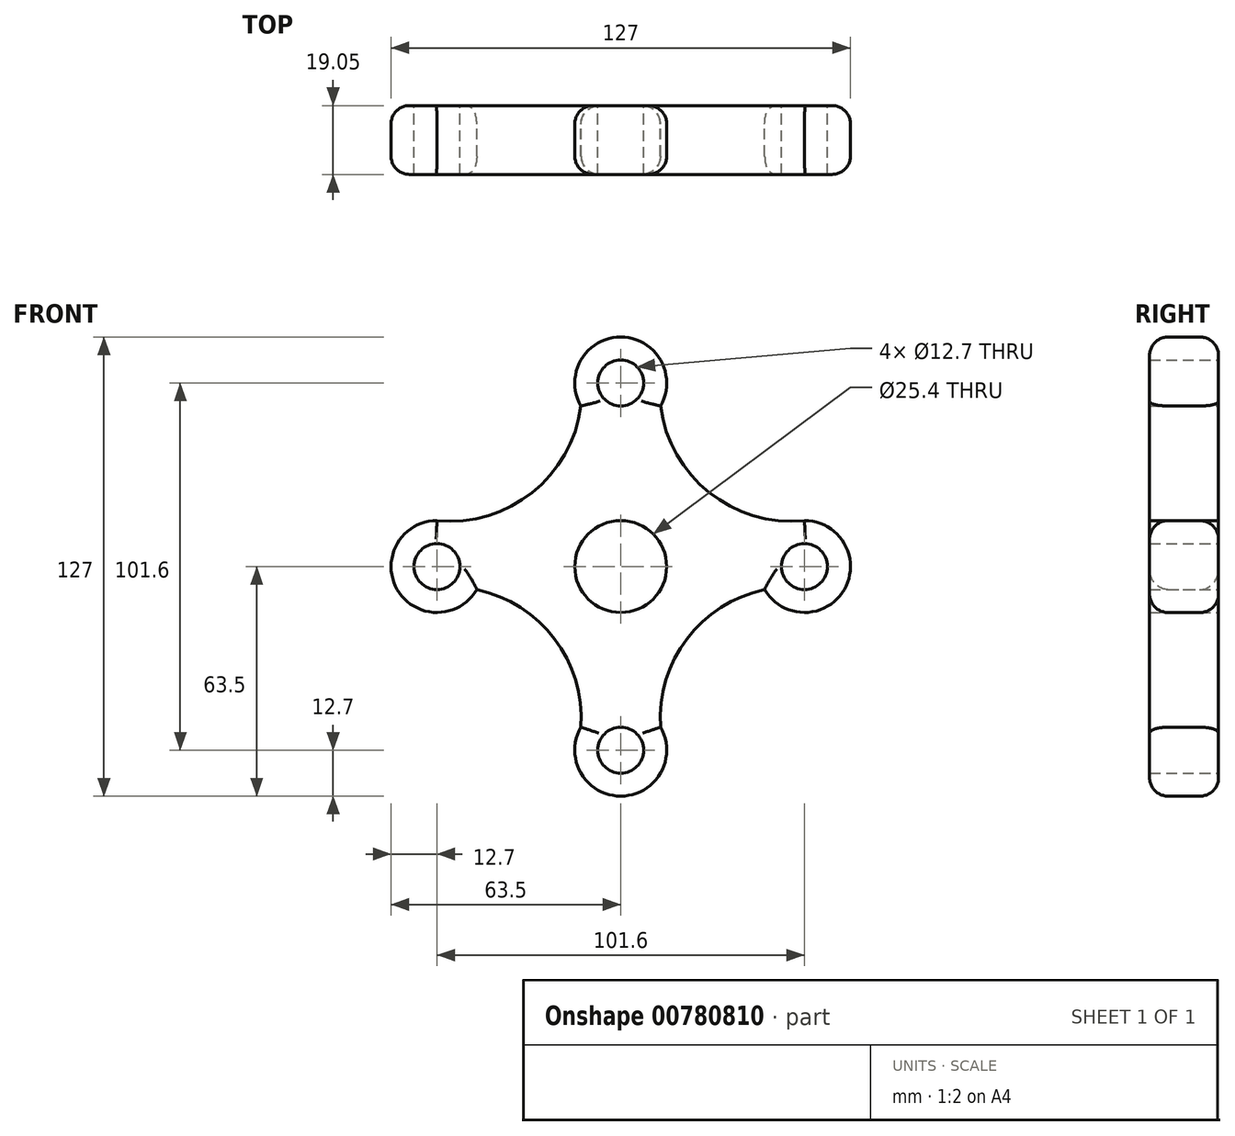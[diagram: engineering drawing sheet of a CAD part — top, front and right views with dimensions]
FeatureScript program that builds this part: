
annotation { "Feature Type Name" : "Feature", "Feature Type Description" : "" }
export const myFeature = defineFeature(function(context is Context, id is Id, definition is map)
    precondition{}
    {
        {
            var Q0;
            Q0=qCreatedBy(makeId("Front.planeOp"),FACE);
            var sketch = newSketch(context, id + "F0", { "sketchPlane" : qUnion([Q0])});
            skCircle(sketch, "E0", {"center": v(0, 0) * mm, "radius": 12.7 * mm});
            skCircle(sketch, "E1", {"center": v(0, 50.8) * mm, "radius": 6.35 * mm});
            skCircle(sketch, "E2", {"center": v(50.8, 0) * mm, "radius": 6.35 * mm});
            skCircle(sketch, "E3", {"center": v(0, -50.8) * mm, "radius": 6.35 * mm});
            skCircle(sketch, "E4", {"center": v(-50.8, 0) * mm, "radius": 6.35 * mm});
            skCircle(sketch, "E5", {"center": v(-50.8, 0) * mm, "radius": 12.7 * mm});
            skCircle(sketch, "E6", {"center": v(0, 50.8) * mm, "radius": 12.7 * mm});
            skCircle(sketch, "E7", {"center": v(50.8, 0) * mm, "radius": 12.7 * mm});
            skCircle(sketch, "E8", {"center": v(0, -50.8) * mm, "radius": 12.7 * mm});
            skLineSegment(sketch, "E9", {"start": v(0, 50.8) * mm, "end": v(0, 50.8) * mm});
            skArc(sketch, "E10", {"start": v(-50.8, 12.7) * mm, "mid": v(-24.45, 20.5) * mm, "end": v(-11, 44.45) * mm});
            skArc(sketch, "E11", {"start": v(11, 44.45) * mm, "mid": v(24.45, 20.5) * mm, "end": v(50.8, 12.7) * mm});
            skArc(sketch, "E12", {"start": v(-11, -44.45) * mm, "mid": v(-18.3, -20.04) * mm, "end": v(-39.8, -6.35) * mm});
            skArc(sketch, "E13", {"start": v(39.8, -6.35) * mm, "mid": v(18.3, -20.04) * mm, "end": v(11, -44.45) * mm});
            skSolve(sketch);
        }
        {
            var Q0;
            {var subQ0=sQuery(id+"F0.wireOp",EDGE,"E13");Q0=makeQuery(id+"F0.imprint","IMPRINT",FACE,{"disambiguationData":[TD([[makeQuery(id+"F0.imprint","IMPRINT",EDGE,{"derivedFrom":subQ0}),-1.0]])]});}
            var Q1;
            {var subQ3=sQuery(id+"F0.wireOp",EDGE,"sHZhk4iH-3IJr-cgO9-yvgX-Rkv4ZYaP15uZ");var subQ5=sQuery(id+"F0.wireOp",EDGE,"E0");var subQ6=makeQuery(id+"F0.imprint","INTERSECT",VERTEX,{"disambiguationData":[OD(0.0)],"derivedFrom":[subQ5,subQ3]});Q1=makeQuery(id+"F0.imprint","IMPRINT",FACE,{"disambiguationData":[TD([[makeQuery(id+"F0.imprint","IMPRINT",EDGE,{"disambiguationData":[TD([[subQ6,1.0]])],"derivedFrom":subQ5}),-1.0]])]});}
            var Q2;
            {var subQ5=sQuery(id+"F0.wireOp",EDGE,"sHZhk4iH-3IJr-cgO9-yvgX-Rkv4ZYaP15uZ");var subQ6=sQuery(id+"F0.wireOp",EDGE,"E0");var subQ7=makeQuery(id+"F0.imprint","INTERSECT",VERTEX,{"disambiguationData":[OD(0.0)],"derivedFrom":[subQ6,subQ5]});Q2=makeQuery(id+"F0.imprint","IMPRINT",FACE,{"disambiguationData":[TD([[makeQuery(id+"F0.imprint","IMPRINT",EDGE,{"disambiguationData":[TD([[subQ7,-1.0]])],"derivedFrom":subQ6}),-1.0]])]});}
            var Q3;
            {var subQ0=sQuery(id+"F0.wireOp",EDGE,"E12");Q3=makeQuery(id+"F0.imprint","IMPRINT",FACE,{"disambiguationData":[TD([[makeQuery(id+"F0.imprint","IMPRINT",EDGE,{"derivedFrom":subQ0}),-1.0]])]});}
            var Q4;
            {var subQ0=sQuery(id+"F0.wireOp",EDGE,"EwxpxNWO-yHll-XO5f-0fvU-fMy1rVfA0yoE");var subQ1=sQuery(id+"F0.wireOp",EDGE,"E4");var subQ2=makeQuery(id+"F0.imprint","INTERSECT",VERTEX,{"derivedFrom":[subQ1,subQ0]});Q4=makeQuery(id+"F0.imprint","IMPRINT",FACE,{"disambiguationData":[TD([[makeQuery(id+"F0.imprint","IMPRINT",EDGE,{"disambiguationData":[TD([[subQ2,-1.0]])],"derivedFrom":subQ1}),-1.0]])]});}
            var Q5;
            {var subQ1=sQuery(id+"F0.wireOp",EDGE,"EwxpxNWO-yHll-XO5f-0fvU-fMy1rVfA0yoE");var subQ4=sQuery(id+"F0.wireOp",EDGE,"E4");var subQ5=makeQuery(id+"F0.imprint","INTERSECT",VERTEX,{"derivedFrom":[subQ4,subQ1]});Q5=makeQuery(id+"F0.imprint","IMPRINT",FACE,{"disambiguationData":[TD([[makeQuery(id+"F0.imprint","IMPRINT",EDGE,{"disambiguationData":[TD([[subQ5,1.0]])],"derivedFrom":subQ4}),-1.0]])]});}
            var Q6;
            {var subQ0=sQuery(id+"F0.wireOp",EDGE,"eux3zpFw-SRj8-7HtN-90hA-iZFYXGH1kXIa");var subQ1=sQuery(id+"F0.wireOp",EDGE,"E4");var subQ2=makeQuery(id+"F0.imprint","INTERSECT",VERTEX,{"derivedFrom":[subQ1,subQ0]});Q6=makeQuery(id+"F0.imprint","IMPRINT",FACE,{"disambiguationData":[TD([[makeQuery(id+"F0.imprint","IMPRINT",EDGE,{"disambiguationData":[TD([[subQ2,-1.0]])],"derivedFrom":subQ1}),-1.0]])]});}
            var Q7;
            {var subQ0=sQuery(id+"F0.wireOp",EDGE,"Hl5PGk0g-RPHx-XJFg-SnUV-gLLTaQPCrOJa");var subQ1=sQuery(id+"F0.wireOp",EDGE,"E4");var subQ2=makeQuery(id+"F0.imprint","INTERSECT",VERTEX,{"derivedFrom":[subQ1,subQ0]});Q7=makeQuery(id+"F0.imprint","IMPRINT",FACE,{"disambiguationData":[TD([[makeQuery(id+"F0.imprint","IMPRINT",EDGE,{"disambiguationData":[TD([[subQ2,1.0]])],"derivedFrom":subQ1}),-1.0]])]});}
            var Q8;
            {var subQ0=sQuery(id+"F0.wireOp",EDGE,"PZf0RJw2-ykNV-p7xf-7yIk-FPkpZ6pm0kLE");var subQ1=sQuery(id+"F0.wireOp",EDGE,"E1");var subQ2=makeQuery(id+"F0.imprint","INTERSECT",VERTEX,{"derivedFrom":[subQ1,subQ0]});Q8=makeQuery(id+"F0.imprint","IMPRINT",FACE,{"disambiguationData":[TD([[makeQuery(id+"F0.imprint","IMPRINT",EDGE,{"disambiguationData":[TD([[subQ2,1.0]])],"derivedFrom":subQ1}),-1.0]])]});}
            var Q9;
            {var subQ0=sQuery(id+"F0.wireOp",EDGE,"hxastzcH-E6gs-Wn1G-Wszv-NTX7wcqDogrz");var subQ1=sQuery(id+"F0.wireOp",EDGE,"E1");var subQ2=makeQuery(id+"F0.imprint","INTERSECT",VERTEX,{"derivedFrom":[subQ1,subQ0]});Q9=makeQuery(id+"F0.imprint","IMPRINT",FACE,{"disambiguationData":[TD([[makeQuery(id+"F0.imprint","IMPRINT",EDGE,{"disambiguationData":[TD([[subQ2,1.0]])],"derivedFrom":subQ1}),-1.0]])]});}
            var Q10;
            {var subQ0=sQuery(id+"F0.wireOp",EDGE,"sHZhk4iH-3IJr-cgO9-yvgX-Rkv4ZYaP15uZ");var subQ1=sQuery(id+"F0.wireOp",EDGE,"E1");var subQ2=makeQuery(id+"F0.imprint","INTERSECT",VERTEX,{"derivedFrom":[subQ1,subQ0]});Q10=makeQuery(id+"F0.imprint","IMPRINT",FACE,{"disambiguationData":[TD([[makeQuery(id+"F0.imprint","IMPRINT",EDGE,{"disambiguationData":[TD([[subQ2,-1.0]])],"derivedFrom":subQ1}),-1.0]])]});}
            var Q11;
            {var subQ0=sQuery(id+"F0.wireOp",EDGE,"sHZhk4iH-3IJr-cgO9-yvgX-Rkv4ZYaP15uZ");var subQ1=sQuery(id+"F0.wireOp",EDGE,"E1");var subQ2=makeQuery(id+"F0.imprint","INTERSECT",VERTEX,{"derivedFrom":[subQ1,subQ0]});Q11=makeQuery(id+"F0.imprint","IMPRINT",FACE,{"disambiguationData":[TD([[makeQuery(id+"F0.imprint","IMPRINT",EDGE,{"disambiguationData":[TD([[subQ2,1.0]])],"derivedFrom":subQ1}),-1.0]])]});}
            var Q12;
            {var subQ0=sQuery(id+"F0.wireOp",EDGE,"HzB6SC3L-xxOl-7oYE-qzgc-gjaryNzKzt03");var subQ1=sQuery(id+"F0.wireOp",EDGE,"E2");var subQ2=makeQuery(id+"F0.imprint","INTERSECT",VERTEX,{"derivedFrom":[subQ1,subQ0]});Q12=makeQuery(id+"F0.imprint","IMPRINT",FACE,{"disambiguationData":[TD([[makeQuery(id+"F0.imprint","IMPRINT",EDGE,{"disambiguationData":[TD([[subQ2,1.0]])],"derivedFrom":subQ1}),-1.0]])]});}
            var Q13;
            {var subQ4=sQuery(id+"F0.wireOp",EDGE,"E2");var subQ7=sQuery(id+"F0.wireOp",EDGE,"Hl5PGk0g-RPHx-XJFg-SnUV-gLLTaQPCrOJa");var subQ9=makeQuery(id+"F0.imprint","INTERSECT",VERTEX,{"derivedFrom":[subQ4,subQ7]});Q13=makeQuery(id+"F0.imprint","IMPRINT",FACE,{"disambiguationData":[TD([[makeQuery(id+"F0.imprint","IMPRINT",EDGE,{"disambiguationData":[TD([[subQ9,1.0]])],"derivedFrom":subQ4}),-1.0]])]});}
            var Q14;
            {var subQ0=sQuery(id+"F0.wireOp",EDGE,"hVdLn5dY-19jR-Z6VQ-oOAF-QHDnoXA8HKQD");var subQ1=sQuery(id+"F0.wireOp",EDGE,"E2");var subQ2=makeQuery(id+"F0.imprint","INTERSECT",VERTEX,{"derivedFrom":[subQ1,subQ0]});Q14=makeQuery(id+"F0.imprint","IMPRINT",FACE,{"disambiguationData":[TD([[makeQuery(id+"F0.imprint","IMPRINT",EDGE,{"disambiguationData":[TD([[subQ2,-1.0]])],"derivedFrom":subQ1}),-1.0]])]});}
            var Q15;
            {var subQ0=sQuery(id+"F0.wireOp",EDGE,"Hl5PGk0g-RPHx-XJFg-SnUV-gLLTaQPCrOJa");var subQ1=sQuery(id+"F0.wireOp",EDGE,"E2");var subQ2=makeQuery(id+"F0.imprint","INTERSECT",VERTEX,{"derivedFrom":[subQ1,subQ0]});Q15=makeQuery(id+"F0.imprint","IMPRINT",FACE,{"disambiguationData":[TD([[makeQuery(id+"F0.imprint","IMPRINT",EDGE,{"disambiguationData":[TD([[subQ2,-1.0]])],"derivedFrom":subQ1}),-1.0]])]});}
            var Q16;
            {var subQ0=sQuery(id+"F0.wireOp",EDGE,"sHZhk4iH-3IJr-cgO9-yvgX-Rkv4ZYaP15uZ");var subQ1=sQuery(id+"F0.wireOp",EDGE,"E3");var subQ2=makeQuery(id+"F0.imprint","INTERSECT",VERTEX,{"derivedFrom":[subQ1,subQ0]});Q16=makeQuery(id+"F0.imprint","IMPRINT",FACE,{"disambiguationData":[TD([[makeQuery(id+"F0.imprint","IMPRINT",EDGE,{"disambiguationData":[TD([[subQ2,1.0]])],"derivedFrom":subQ1}),-1.0]])]});}
            var Q17;
            {var subQ0=sQuery(id+"F0.wireOp",EDGE,"sHZhk4iH-3IJr-cgO9-yvgX-Rkv4ZYaP15uZ");var subQ1=sQuery(id+"F0.wireOp",EDGE,"E3");var subQ2=makeQuery(id+"F0.imprint","INTERSECT",VERTEX,{"derivedFrom":[subQ1,subQ0]});Q17=makeQuery(id+"F0.imprint","IMPRINT",FACE,{"disambiguationData":[TD([[makeQuery(id+"F0.imprint","IMPRINT",EDGE,{"disambiguationData":[TD([[subQ2,-1.0]])],"derivedFrom":subQ1}),-1.0]])]});}
            var Q18;
            {var subQ0=sQuery(id+"F0.wireOp",EDGE,"FXrztN1G-Fvm6-87nT-5k1E-FaQXGZbOXUzD");var subQ1=sQuery(id+"F0.wireOp",EDGE,"E3");var subQ2=makeQuery(id+"F0.imprint","INTERSECT",VERTEX,{"derivedFrom":[subQ1,subQ0]});Q18=makeQuery(id+"F0.imprint","IMPRINT",FACE,{"disambiguationData":[TD([[makeQuery(id+"F0.imprint","IMPRINT",EDGE,{"disambiguationData":[TD([[subQ2,-1.0]])],"derivedFrom":subQ1}),-1.0]])]});}
            var Q19;
            {var subQ0=sQuery(id+"F0.wireOp",EDGE,"j56TRUOZ-1Wll-gAmP-n2iP-PXOIl2fHJL6b");var subQ1=sQuery(id+"F0.wireOp",EDGE,"E3");var subQ2=makeQuery(id+"F0.imprint","INTERSECT",VERTEX,{"derivedFrom":[subQ1,subQ0]});Q19=makeQuery(id+"F0.imprint","IMPRINT",FACE,{"disambiguationData":[TD([[makeQuery(id+"F0.imprint","IMPRINT",EDGE,{"disambiguationData":[TD([[subQ2,1.0]])],"derivedFrom":subQ1}),-1.0]])]});}
            extrude(context, id + "F1", {"entities" : qUnion([Q0, Q1, Q2, Q3, Q4, Q5, Q6, Q7, Q8, Q9, Q10, Q11, Q12, Q13, Q14, Q15, Q16, Q17, Q18, Q19]), "depth" : 19.05 * mm, "offsetDistance" : 25.4 * mm});
        }
        {
            var Q0;
            Q0=makeQuery(id+"F1.opExtrude","CAP_EDGE",EDGE,{"disambiguationData":[OSD([sQuery(id+"F0.wireOp",EDGE,"E6")])],"isStart":false});
            var Q1;
            Q1=makeQuery(id+"F1.opExtrude","CAP_EDGE",EDGE,{"disambiguationData":[OSD([sQuery(id+"F0.wireOp",EDGE,"E10")])],"isStart":false});
            var Q2;
            Q2=makeQuery(id+"F1.opExtrude","CAP_EDGE",EDGE,{"disambiguationData":[OSD([sQuery(id+"F0.wireOp",EDGE,"E5")])],"isStart":false});
            var Q3;
            Q3=makeQuery(id+"F1.opExtrude","CAP_EDGE",EDGE,{"disambiguationData":[OSD([sQuery(id+"F0.wireOp",EDGE,"E12")])],"isStart":false});
            var Q4;
            Q4=makeQuery(id+"F1.opExtrude","CAP_EDGE",EDGE,{"disambiguationData":[OSD([sQuery(id+"F0.wireOp",EDGE,"E8")])],"isStart":false});
            var Q5;
            Q5=makeQuery(id+"F1.opExtrude","CAP_EDGE",EDGE,{"disambiguationData":[OSD([sQuery(id+"F0.wireOp",EDGE,"E13")])],"isStart":false});
            var Q6;
            Q6=makeQuery(id+"F1.opExtrude","CAP_EDGE",EDGE,{"disambiguationData":[OSD([sQuery(id+"F0.wireOp",EDGE,"E7")])],"isStart":false});
            var Q7;
            Q7=makeQuery(id+"F1.opExtrude","CAP_EDGE",EDGE,{"disambiguationData":[OSD([sQuery(id+"F0.wireOp",EDGE,"E11")])],"isStart":false});
            fillet(context, id + "F2", {"entities" : qUnion([Q0, Q1, Q2, Q3, Q4, Q5, Q6, Q7]), "radius" : 5.08 * mm, "tangentPropagation" : true, "allowEdgeOverflow" : false});
        }
        {
            var Q0;
            Q0=makeQuery(id+"F1.opExtrude","CAP_EDGE",EDGE,{"disambiguationData":[OSD([sQuery(id+"F0.wireOp",EDGE,"E8")])],"isStart":true});
            var Q1;
            Q1=makeQuery(id+"F1.opExtrude","CAP_EDGE",EDGE,{"disambiguationData":[OSD([sQuery(id+"F0.wireOp",EDGE,"E13")])],"isStart":true});
            var Q2;
            Q2=makeQuery(id+"F1.opExtrude","CAP_EDGE",EDGE,{"disambiguationData":[OSD([sQuery(id+"F0.wireOp",EDGE,"E7")])],"isStart":true});
            var Q3;
            Q3=makeQuery(id+"F1.opExtrude","CAP_EDGE",EDGE,{"disambiguationData":[OSD([sQuery(id+"F0.wireOp",EDGE,"E11")])],"isStart":true});
            var Q4;
            Q4=makeQuery(id+"F1.opExtrude","CAP_EDGE",EDGE,{"disambiguationData":[OSD([sQuery(id+"F0.wireOp",EDGE,"E6")])],"isStart":true});
            var Q5;
            Q5=makeQuery(id+"F1.opExtrude","CAP_EDGE",EDGE,{"disambiguationData":[OSD([sQuery(id+"F0.wireOp",EDGE,"E10")])],"isStart":true});
            var Q6;
            Q6=makeQuery(id+"F1.opExtrude","CAP_EDGE",EDGE,{"disambiguationData":[OSD([sQuery(id+"F0.wireOp",EDGE,"E5")])],"isStart":true});
            var Q7;
            Q7=makeQuery(id+"F1.opExtrude","CAP_EDGE",EDGE,{"disambiguationData":[OSD([sQuery(id+"F0.wireOp",EDGE,"E12")])],"isStart":true});
            fillet(context, id + "F3", {"entities" : qUnion([Q0, Q1, Q2, Q3, Q4, Q5, Q6, Q7]), "radius" : 5.08 * mm, "tangentPropagation" : true, "allowEdgeOverflow" : false});
        }
    });
